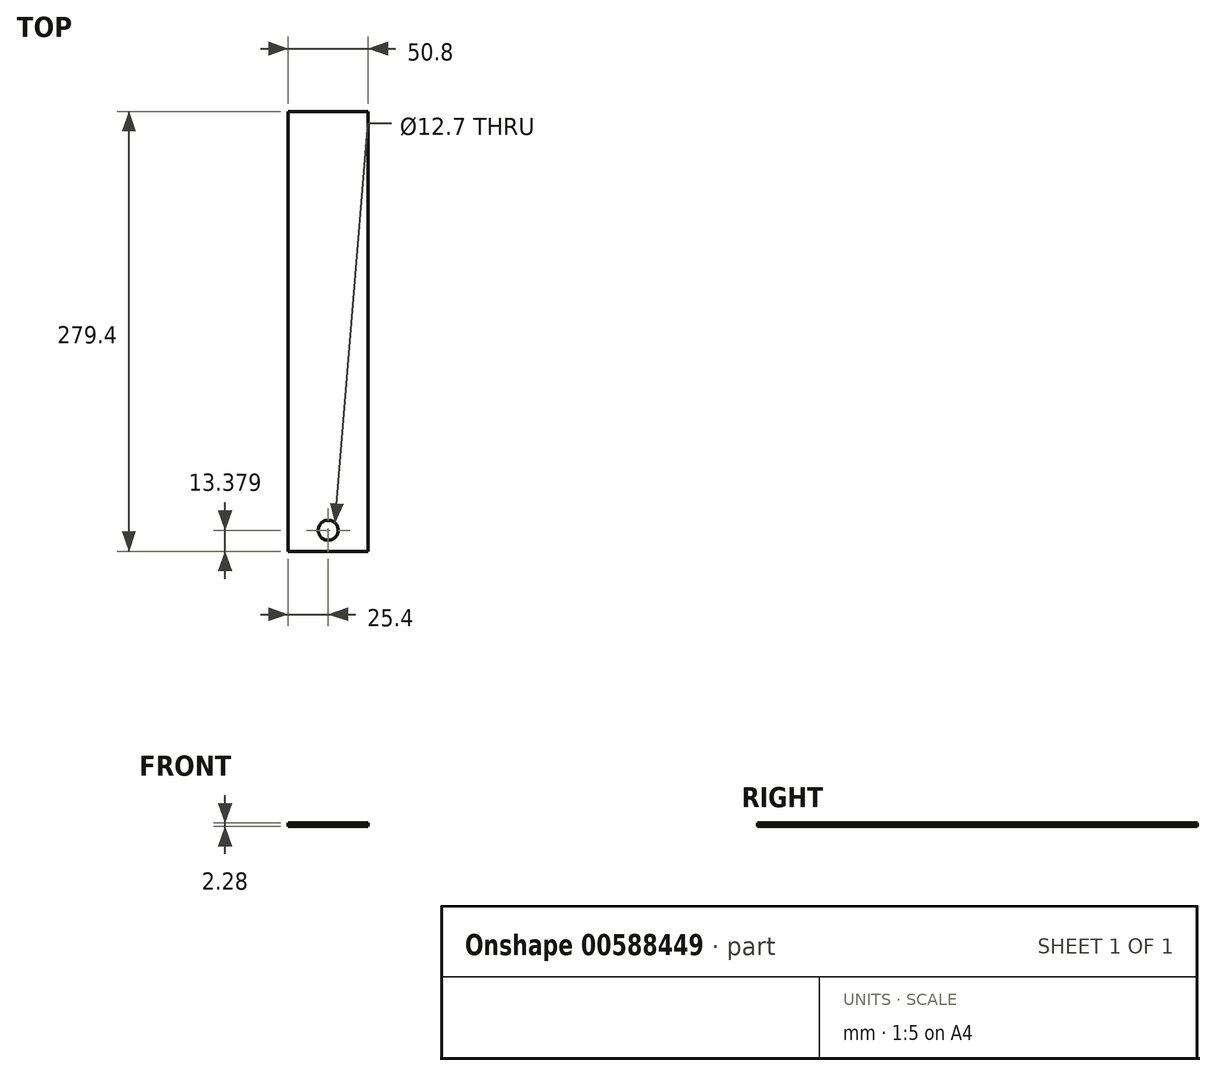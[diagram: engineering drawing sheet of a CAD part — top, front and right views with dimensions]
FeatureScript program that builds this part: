
annotation { "Feature Type Name" : "Feature", "Feature Type Description" : "" }
export const myFeature = defineFeature(function(context is Context, id is Id, definition is map)
    precondition{}
    {
        {
            var Q0;
            Q0=qCreatedBy(makeId("Front.planeOp"),FACE);
            var sketch = newSketch(context, id + "F0", { "sketchPlane" : qUnion([Q0])});
            skLineSegment(sketch, "E0.bottom", {"start": v(-25.4, 1.14) * mm, "end": v(25.4, 1.14) * mm});
            skLineSegment(sketch, "E0.top", {"start": v(-25.4, -1.14) * mm, "end": v(25.4, -1.14) * mm});
            skLineSegment(sketch, "E0.left", {"start": v(-25.4, 1.14) * mm, "end": v(-25.4, -1.14) * mm});
            skLineSegment(sketch, "E0.right", {"start": v(25.4, 1.14) * mm, "end": v(25.4, -1.14) * mm});
            skPoint(sketch, "E0.middle", {"position": v(0, 0) * mm});
            skSolve(sketch);
        }
        {
            var Q0;
            Q0=makeQuery(id+"F0.imprint","IMPRINT",FACE,{"disambiguationData":[TD([[makeQuery(id+"F0.imprint","IMPRINT",EDGE,{"derivedFrom":sQuery(id+"F0.wireOp",EDGE,"E0.bottom")}),-1.0]])]});
            extrude(context, id + "F1", {"entities" : qUnion([Q0]), "endBound" : BoundingType.SYMMETRIC, "depth" : 279.4 * mm, "offsetDistance" : 25.4 * mm});
        }
        {
            var Q0;
            Q0=makeQuery(id+"F1.opExtrude","SWEPT_FACE",FACE,{"disambiguationData":[OSD([sQuery(id+"F0.wireOp",EDGE,"E0.bottom")])]});
            var sketch = newSketch(context, id + "F2", { "sketchPlane" : qUnion([Q0])});
            skCircle(sketch, "E1", {"center": v(0, -126.32) * mm, "radius": 8.07 * mm});
            skSolve(sketch);
        }
        {
            var Q0;
            Q0=sQuery(id+"F2.wireOp",VERTEX,"E1.center");
            var Q1;
            Q1=makeQuery(id+"F1.opExtrude","SWEPT_BODY",BODY,{"disambiguationData":[OSD([sQuery(id+"F0.wireOp",EDGE,"E0.bottom"),sQuery(id+"F0.wireOp",EDGE,"E0.top"),sQuery(id+"F0.wireOp",EDGE,"E0.left"),sQuery(id+"F0.wireOp",EDGE,"E0.right")])]});
            hole(context, id + "F3", {"style" : HoleStyle.SIMPLE, "endStyle" : HoleEndStyle.THROUGH, "holeDiameter" : 12.7 * mm, "majorDiameter" : 6.35 * mm, "isTappedThrough" : true, "tappedDepth" : 12.7 * mm, "tapClearance" : 3, "locations" : qUnion([Q0]), "scope" : qUnion([Q1])});
        }
    });
